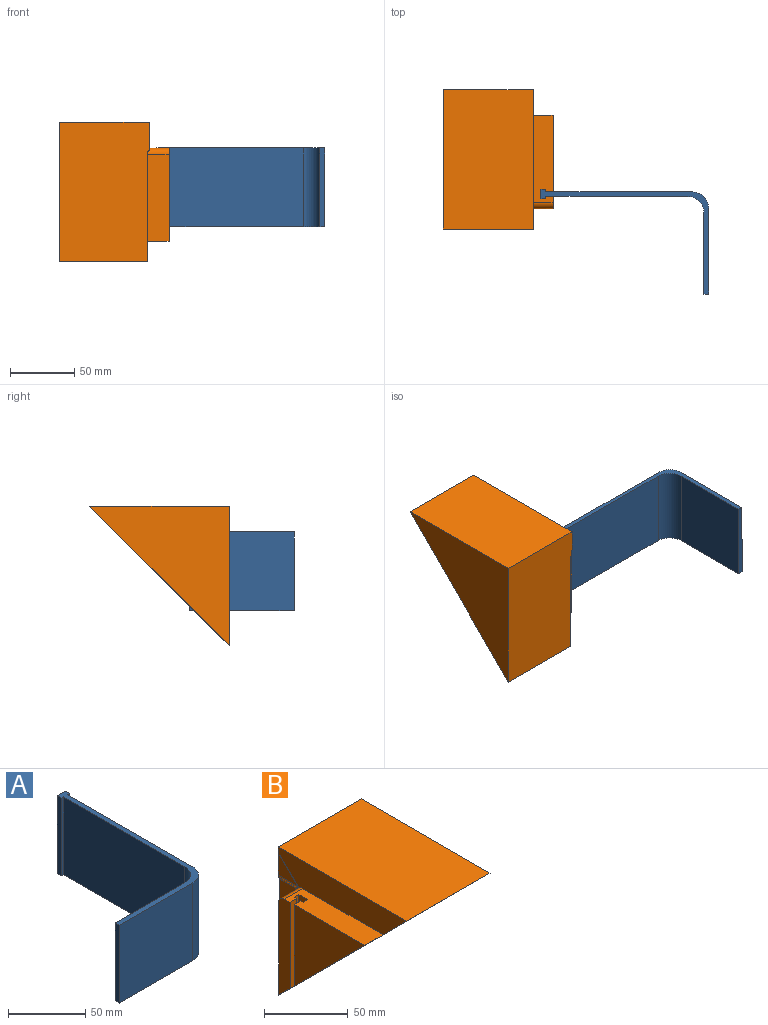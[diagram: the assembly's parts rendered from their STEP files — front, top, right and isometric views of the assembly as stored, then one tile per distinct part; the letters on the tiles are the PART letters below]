
ASSEMBLY  parts=2 mates=1
PART A: 14 faces, bbox 81.7x130.8x61.5 mm
  f0: plane 110.55x61.47mm, normal (-1,0,0), area 6795.5mm2, adj f9,f10,f11,f12
  f1: plane 63.5x61.47mm, normal (0,1,0), area 3903.2mm2, adj f2,f10,f11,f12
  f2: plane 61.47x3.75mm, normal (-1,0,0), area 230.3mm2, adj f1,f3,f10,f11
  f3: plane 66.93x61.47mm, normal (0,-1,0), area 4114mm2, adj f2,f10,f11,f13
  f4: plane 114.3x61.47mm, normal (1,0,0), area 7025.8mm2, adj f5,f10,f11,f13
  f5: plane 61.47x2.03mm, normal (0,-1,0), area 124.9mm2, adj f4,f6,f10,f11
  f6: plane 61.47x3.81mm, normal (1,0,0), area 234.2mm2, adj f5,f7,f10,f11
  f7: plane 61.47x7.49mm, normal (0,1,0), area 460.6mm2, adj f6,f8,f10,f11
  f8: plane 61.47x3.81mm, normal (-1,0,0), area 234.2mm2, adj f7,f9,f10,f11
  f9: plane 61.47x2.03mm, normal (0,-1,0), area 124.9mm2, adj f0,f8,f10,f11
  f10: plane 130.81x81.66mm, normal (0,0,1), area 749.5mm2, adj f0,f1,f2,f3,f4,f5,f6,f7
  f11: plane 130.81x81.66mm, normal (0,0,-1), area 749.5mm2, adj f0,f1,f2,f3,f4,f5,f6,f7
  f12: cylinder r=12.7mm len=61.47mm, axis (0,0,1), area 1226.2mm2, adj f0,f1,f10,f11
  f13: cylinder r=12.7mm len=61.47mm, axis (0,0,-1), area 1226.2mm2, adj f3,f4,f10,f11
PART B: 32 faces, bbox 85.6x108.6x108.6 mm
  f0: plane 72.7x9.68mm, normal (-1,0,0), area 651.3mm2, adj f1,f2,f21,f24,f25
  f1: plane 108.56x108.56mm, normal (0,-0.71,-0.71), area 5428.4mm2, adj f0,f2,f3,f4,f7,f11,f12,f13
  f2: plane 67.62x15.42mm, normal (0,0,1), area 994.7mm2, adj f0,f1,f3,f7,f24,f25,f26,f27
  f3: plane 59.58x59.58mm, normal (-1,0,0), area 1774.7mm2, adj f1,f2,f26
  f4: plane 84.28x15.9mm, normal (-1,0,0), area 1213.6mm2, adj f1,f12,f17,f21
  f5: plane 4.8x1.16mm, normal (0,-1,0), area 3.6mm2, adj f6,f8,f22,f23
  f6: cylinder r=2.54mm len=2.51mm, axis (-1,0,0), area 2.3mm2, adj f5,f8,f18,f23
  f7: plane 108.61x21.26mm, normal (-1,0,0), area 1837.4mm2, adj f1,f2,f9,f10,f11,f12,f24
  f8: bspline ~3.61x2.81mm, area 5.2mm2, adj f5,f6,f17,f18,f22,f23
  f9: cylinder r=2.54mm len=17.28mm, axis (0,-0.71,-0.71), area 8.7mm2, adj f7,f10,f16,f17,f24
  f10: plane 16.69x15.25mm, normal (-1,0,0), area 137.5mm2, adj f7,f9,f12,f16
  f11: plane 108.56x70.18mm, normal (0,0,1), area 7618.7mm2, adj f1,f7,f12,f20
  f12: plane 108.56x70.18mm, normal (0,1,0), area 7489.2mm2, adj f1,f4,f7,f10,f11,f16,f17,f20
  f13: plane 101.68x47.5mm, normal (0,0,-1), area 4829.4mm2, adj f1,f14,f15,f19
  f14: plane 101.68x101.68mm, normal (1,0,0), area 5169mm2, adj f1,f13,f15
  f15: plane 101.68x47.5mm, normal (0,-1,0), area 4829.4mm2, adj f1,f13,f14,f19
  f16: cylinder r=2.54mm len=16.64mm, axis (0,-1,0), area 32.8mm2, adj f9,f10,f12,f17
  f17: cylinder r=2.54mm len=18.95mm, axis (0,-1,0), area 39.9mm2, adj f4,f8,f9,f12,f16,f18,f21,f22
  f18: bspline ~3.1x2.32mm, area 0.7mm2, adj f6,f8,f17
  f19: plane 101.68x101.68mm, normal (-1,0,0), area 5169mm2, adj f1,f13,f15
  f20: plane 108.56x108.56mm, normal (1,0,0), area 5892.6mm2, adj f1,f11,f12
  f21: plane 68.37x16.92mm, normal (0,1,0), area 1143.8mm2, adj f0,f1,f4,f17,f22,f24
  f22: plane 3.08x2.57mm, normal (1,0,0), area 7.4mm2, adj f5,f8,f17,f21,f24
  f23: plane 4.8x2.17mm, normal (1,0,0), area 4.7mm2, adj f5,f6,f8
  f24: cylinder r=5.08mm len=16.58mm, axis (-1,0,0), area 126.4mm2, adj f0,f2,f7,f9,f17,f21,f22
  f25: plane 63.01x5.59mm, normal (0,-1,0), area 352.1mm2, adj f0,f1,f2,f31
  f26: plane 59.58x5.59mm, normal (0,1,0), area 332.9mm2, adj f1,f2,f3,f27
  f27: plane 59.58x2.03mm, normal (1,0,0), area 119mm2, adj f1,f2,f26,f28
  f28: plane 57.54x3.81mm, normal (0,1,0), area 219.2mm2, adj f1,f2,f27,f29
  f29: plane 65.05x7.5mm, normal (-1,0,0), area 459.9mm2, adj f1,f2,f28,f30
  f30: plane 65.05x3.81mm, normal (0,-1,0), area 247.8mm2, adj f1,f2,f29,f31
  f31: plane 65.05x2.03mm, normal (1,0,0), area 130.1mm2, adj f1,f2,f25,f30
PLACE A rot(axis=(0,0,1),90deg) t=(-42.54,-40.08,1.06)mm
PLACE B rot(axis=(0,0,1),180deg) t=(-104.06,37.46,-24.66)mm
MATE fastened A.f7 <-> B.f29  axis (-1,0,0) through (-49.96,-38.37,31.8)mm
